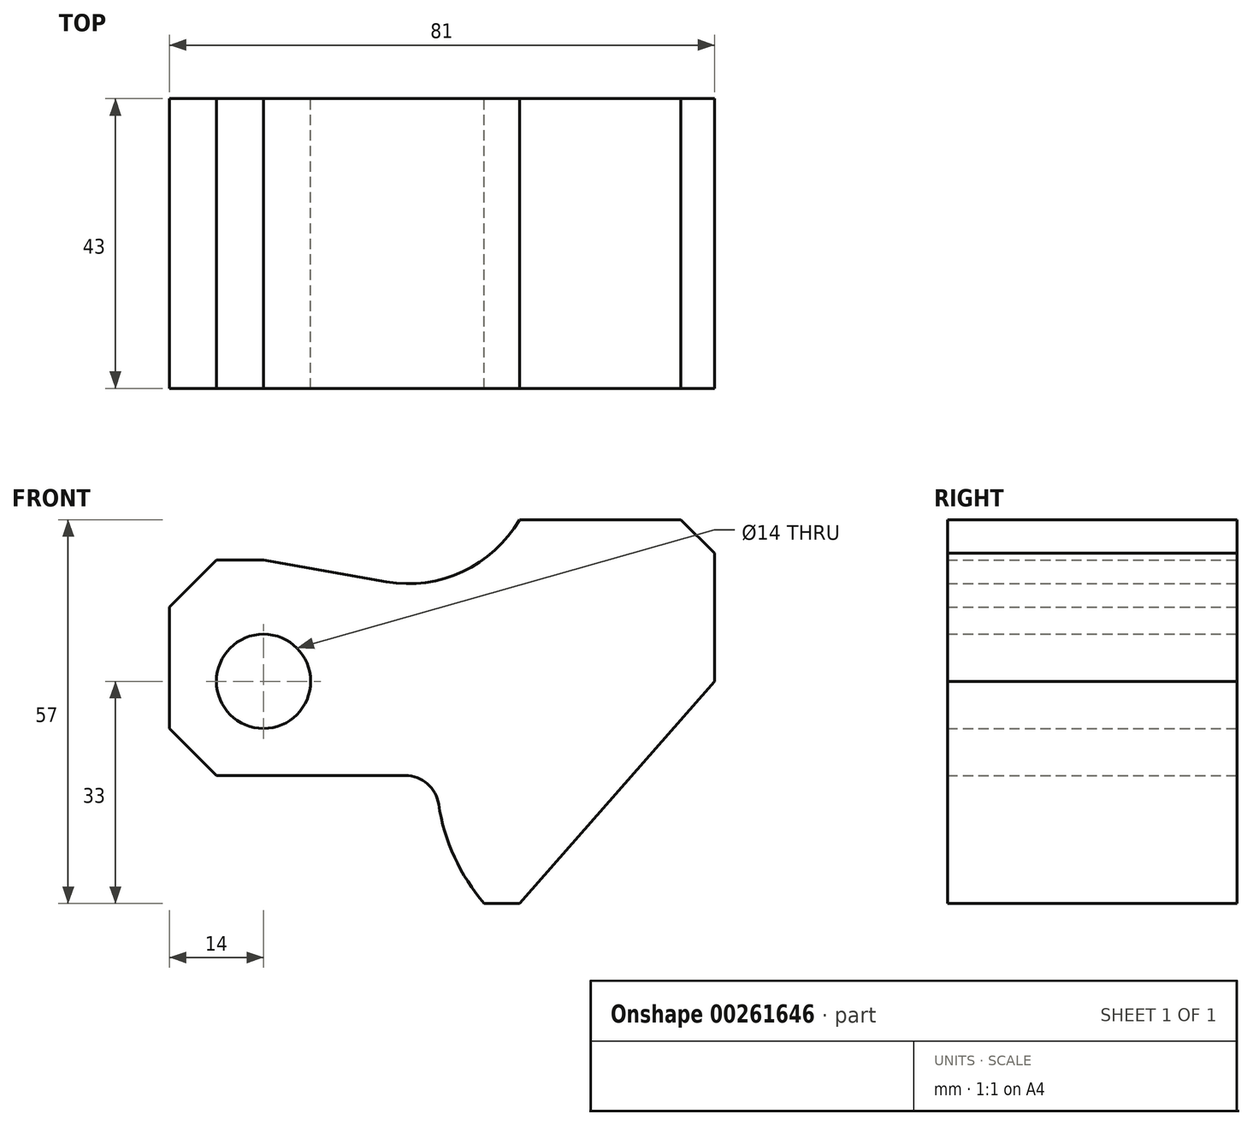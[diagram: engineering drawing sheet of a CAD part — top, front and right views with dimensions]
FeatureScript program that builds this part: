
annotation { "Feature Type Name" : "Feature", "Feature Type Description" : "" }
export const myFeature = defineFeature(function(context is Context, id is Id, definition is map)
    precondition{}
    {
        {
            var Q0;
            Q0=qCreatedBy(makeId("Front.planeOp"),FACE);
            var sketch = newSketch(context, id + "F0", { "sketchPlane" : qUnion([Q0])});
            skLineSegment(sketch, "E0.bottom", {"start": v(40.5, 28.5) * mm, "end": v(-40.5, 28.5) * mm, "construction": true});
            skLineSegment(sketch, "E0.top", {"start": v(40.5, -28.5) * mm, "end": v(-40.5, -28.5) * mm, "construction": true});
            skLineSegment(sketch, "E0.left", {"start": v(40.5, 28.5) * mm, "end": v(40.5, -28.5) * mm, "construction": true});
            skLineSegment(sketch, "E0.right", {"start": v(-40.5, 28.5) * mm, "end": v(-40.5, -28.5) * mm, "construction": true});
            skPoint(sketch, "E0.middle", {"position": v(0, 0) * mm});
            skLineSegment(sketch, "E1", {"start": v(11.5, -28.5) * mm, "end": v(40.5, 4.5) * mm});
            skLineSegment(sketch, "E2", {"start": v(35.5, 28.5) * mm, "end": v(40.5, 23.5) * mm});
            skLineSegment(sketch, "E3", {"start": v(40.5, 23.5) * mm, "end": v(40.5, 4.5) * mm});
            skArc(sketch, "E4", {"start": v(-0.49, -13.76) * mm, "mid": v(1.85, -21.62) * mm, "end": v(6.29, -28.5) * mm});
            skLineSegment(sketch, "E5", {"start": v(11.5, -28.5) * mm, "end": v(6.29, -28.5) * mm});
            skLineSegment(sketch, "E6", {"start": v(35.5, 28.5) * mm, "end": v(-40.5, 28.5) * mm});
            skLineSegment(sketch, "E7", {"start": v(-33.5, -9.5) * mm, "end": v(-40.5, -2.5) * mm});
            skArc(sketch, "E8", {"start": v(-0.49, -13.76) * mm, "mid": v(-2.17, -10.71) * mm, "end": v(-5.43, -9.5) * mm});
            skLineSegment(sketch, "E9.trimOffspring", {"start": v(-5.43, -9.5) * mm, "end": v(-33.5, -9.5) * mm});
            skLineSegment(sketch, "E10", {"start": v(-40.5, -2.5) * mm, "end": v(-40.5, 15.5) * mm});
            skLineSegment(sketch, "E11", {"start": v(-40.5, 15.5) * mm, "end": v(-33.5, 22.5) * mm});
            skLineSegment(sketch, "E12", {"start": v(-33.5, 22.5) * mm, "end": v(-26.5, 22.5) * mm});
            skLineSegment(sketch, "E13", {"start": v(-26.5, 22.5) * mm, "end": v(-8.26, 19.28) * mm});
            skArc(sketch, "E14", {"start": v(-8.26, 19.28) * mm, "mid": v(3.07, 20.78) * mm, "end": v(11.5, 28.5) * mm});
            skCircle(sketch, "E15", {"center": v(-26.5, 4.5) * mm, "radius": 7 * mm});
            skSolve(sketch);
        }
        {
            var Q0;
            Q0=makeQuery(id+"F0.imprint","IMPRINT",FACE,{"disambiguationData":[TD([[makeQuery(id+"F0.imprint","IMPRINT",EDGE,{"derivedFrom":sQuery(id+"F0.wireOp",EDGE,"E1")}),1.0]])]});
            extrude(context, id + "F1", {"entities" : qUnion([Q0]), "depth" : 43 * mm});
        }
    });
